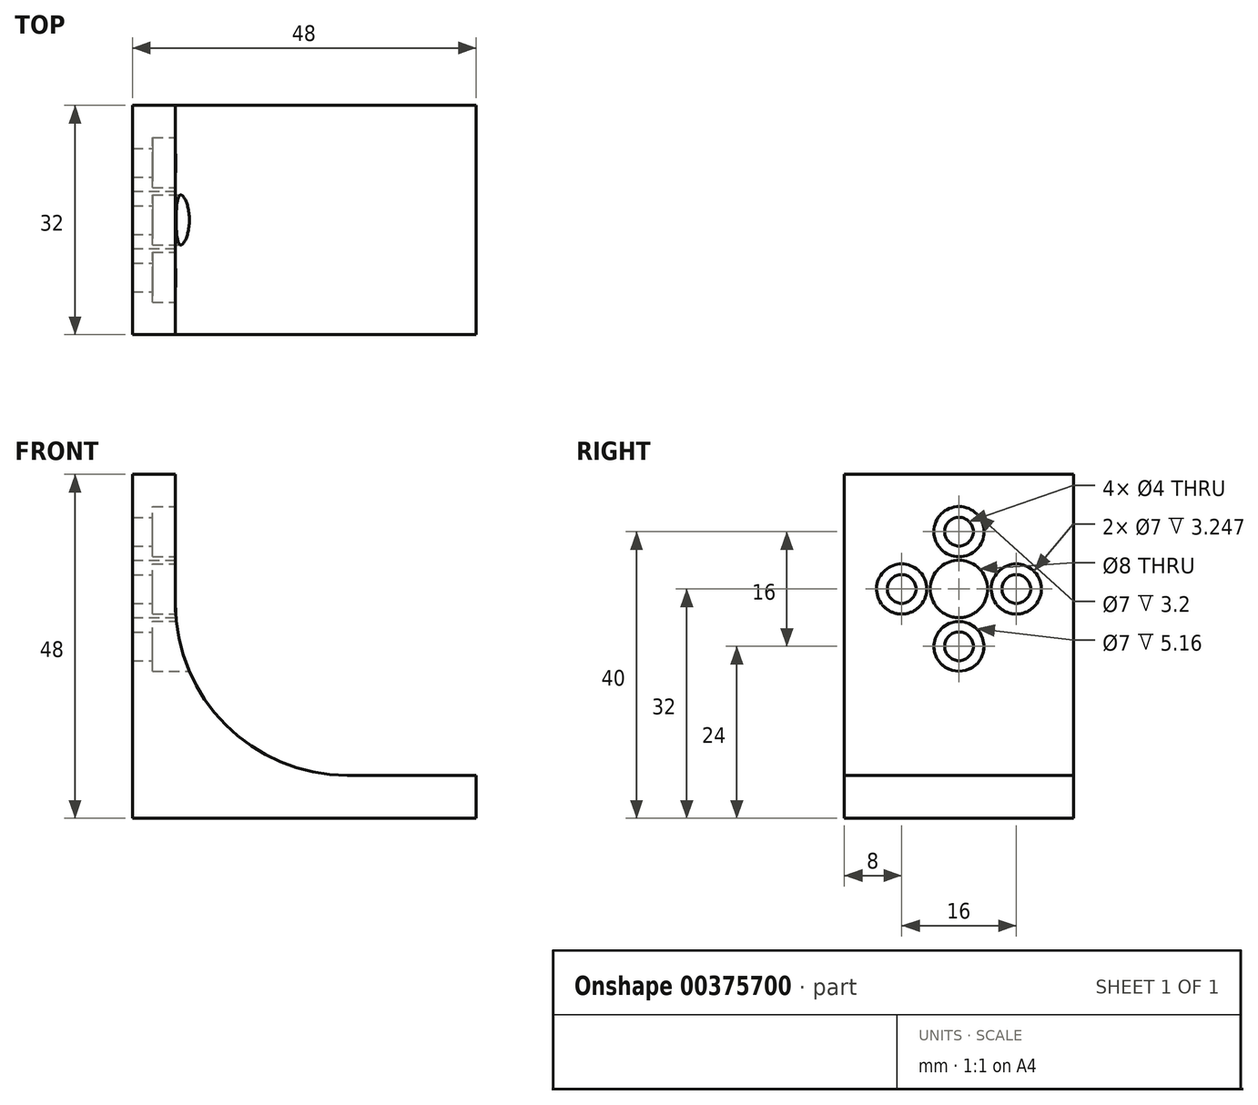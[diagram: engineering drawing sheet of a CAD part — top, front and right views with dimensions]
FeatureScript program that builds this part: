
annotation { "Feature Type Name" : "Feature", "Feature Type Description" : "" }
export const myFeature = defineFeature(function(context is Context, id is Id, definition is map)
    precondition{}
    {
        {
            assignVariable(context, id + "F0", {"name" : "Extrusion", "anyValue" : 0.4});
        }
        {
            assignVariable(context, id + "F1", {"name" : "Shells", "anyValue" : 3});
        }
        {
            assignVariable(context, id + "F2", {"name" : "Wall", "anyValue" : getVariable(context, 'Extrusion') * (getVariable(context, 'Shells') * 2 + 1)});
        }
        {
            assignVariable(context, id + "F3", {"name" : "Frame", "anyValue" : 6});
        }
        {
            var Q0;
            Q0=qCreatedBy(makeId("Front.planeOp"),FACE);
            var sketch = newSketch(context, id + "F4", { "sketchPlane" : qUnion([Q0])});
            skLineSegment(sketch, "E0", {"start": v(0, 48) * mm, "end": v(0, 0) * mm});
            skLineSegment(sketch, "E1", {"start": v(0, 0) * mm, "end": v(48, 0) * mm});
            skCircle(sketch, "E2", {"center": v(0, 0) * mm, "radius": 4 * mm, "construction": true});
            skCircle(sketch, "E3", {"center": v(16, 0) * mm, "radius": 4 * mm, "construction": true});
            skCircle(sketch, "E4", {"center": v(32, 0) * mm, "radius": 4 * mm, "construction": true});
            skCircle(sketch, "E5", {"center": v(0, 16) * mm, "radius": 4 * mm, "construction": true});
            skCircle(sketch, "E6", {"center": v(0, 32) * mm, "radius": 4 * mm, "construction": true});
            skLineSegment(sketch, "E7", {"start": v(0, 48) * mm, "end": v(6, 48) * mm});
            skLineSegment(sketch, "E8", {"start": v(48, 0) * mm, "end": v(48, 6) * mm});
            skArc(sketch, "E9", {"start": v(6, 48) * mm, "mid": v(18.3, 18.3) * mm, "end": v(48, 6) * mm});
            skLineSegment(sketch, "E10", {"start": v(6, 48) * mm, "end": v(6, 6) * mm});
            skLineSegment(sketch, "E11", {"start": v(6, 6) * mm, "end": v(48, 6) * mm});
            skSolve(sketch);
        }
        {
            var Q0;
            Q0=makeQuery(id+"F4.imprint","IMPRINT",FACE,{"disambiguationData":[TD([[makeQuery(id+"F4.imprint","IMPRINT",EDGE,{"derivedFrom":sQuery(id+"F4.wireOp",EDGE,"E0")}),1.0]])]});
            extrude(context, id + "F5", {"entities" : qUnion([Q0]), "endBound" : BoundingType.SYMMETRIC, "depth" : 32 * mm});
        }
        {
            var Q0;
            Q0=makeQuery(id+"F5.opExtrude","SWEPT_FACE",FACE,{"disambiguationData":[OSD([sQuery(id+"F4.wireOp",EDGE,"E10")])]});
            var sketch = newSketch(context, id + "F6", { "sketchPlane" : qUnion([Q0])});
            skPoint(sketch, "E12.0", {"position": v(0, 32) * mm});
            skCircle(sketch, "E13", {"center": v(0, 32) * mm, "radius": 4 * mm});
            skCircle(sketch, "E14", {"center": v(0, 40) * mm, "radius": 2 * mm});
            skCircle(sketch, "E15.1.0", {"center": v(-8, 32) * mm, "radius": 2 * mm});
            skCircle(sketch, "E15.2.0", {"center": v(0, 24) * mm, "radius": 2 * mm});
            skCircle(sketch, "E15.3.0", {"center": v(8, 32) * mm, "radius": 2 * mm});
            skCircle(sketch, "E16", {"center": v(0, 40) * mm, "radius": 3.5 * mm});
            skCircle(sketch, "E17", {"center": v(8, 32) * mm, "radius": 3.5 * mm});
            skCircle(sketch, "E18", {"center": v(0, 24) * mm, "radius": 3.5 * mm});
            skCircle(sketch, "E19", {"center": v(-8, 32) * mm, "radius": 3.5 * mm});
            skSolve(sketch);
        }
        {
            var Q0;
            Q0=makeQuery(id+"F5.opExtrude","SWEPT_EDGE",EDGE,{"disambiguationData":[OSD([sQuery(id+"F4.wireOp",EDGE,"E10"),sQuery(id+"F4.wireOp",EDGE,"E11")])]});
            fillet(context, id + "F7", {"entities" : qUnion([Q0]), "radius" : (getVariable(context, 'Frame') * 4) * mm, "tangentPropagation" : true, "allowEdgeOverflow" : false});
        }
        {
            var Q0;
            Q0=makeQuery(id+"F6.imprint","IMPRINT",FACE,{"disambiguationData":[TD([[makeQuery(id+"F6.imprint","IMPRINT",EDGE,{"derivedFrom":sQuery(id+"F6.wireOp",EDGE,"E15.1.0")}),1.0]])]});
            var Q1;
            Q1=makeQuery(id+"F6.imprint","IMPRINT",FACE,{"disambiguationData":[TD([[makeQuery(id+"F6.imprint","IMPRINT",EDGE,{"derivedFrom":sQuery(id+"F6.wireOp",EDGE,"E14")}),1.0]])]});
            var Q2;
            Q2=makeQuery(id+"F6.imprint","IMPRINT",FACE,{"disambiguationData":[TD([[makeQuery(id+"F6.imprint","IMPRINT",EDGE,{"derivedFrom":sQuery(id+"F6.wireOp",EDGE,"E15.3.0")}),1.0]])]});
            var Q3;
            Q3=makeQuery(id+"F6.imprint","IMPRINT",FACE,{"disambiguationData":[TD([[makeQuery(id+"F6.imprint","IMPRINT",EDGE,{"derivedFrom":sQuery(id+"F6.wireOp",EDGE,"E13")}),1.0]])]});
            var Q4;
            Q4=makeQuery(id+"F6.imprint","IMPRINT",FACE,{"disambiguationData":[TD([[makeQuery(id+"F6.imprint","IMPRINT",EDGE,{"derivedFrom":sQuery(id+"F6.wireOp",EDGE,"E15.2.0")}),1.0]])]});
            extrude(context, id + "F8", {"entities" : qUnion([Q0, Q1, Q2, Q3, Q4]), "operationType" : NewBodyOperationType.REMOVE, "endBound" : BoundingType.THROUGH_ALL, "oppositeDirection" : true, "depth" : 25 * mm, "hasSecondDirection" : true, "secondDirectionBound" : SecondDirectionBoundingType.THROUGH_ALL, "secondDirectionOppositeDirection" : false, "secondDirectionDepth" : 25 * mm});
        }
        {
            var Q0;
            {var subQ0=sQuery(id+"F6.wireOp",EDGE,"E15.1.0");Q0=makeQuery(id+"F6.imprint","IMPRINT",FACE,{"disambiguationData":[TD([[makeQuery(id+"F6.imprint","IMPRINT",EDGE,{"derivedFrom":subQ0}),-1.0]])]});}
            var Q1;
            {var subQ0=sQuery(id+"F6.wireOp",EDGE,"E19");var subQ1=sQuery(id+"F4.wireOp",EDGE,"E0");var subQ2=makeQuery(id+"FzLZcs18jVHRiGl_1.opShell","OFFSET_EDGE",EDGE,{"disambiguationData":[OSD([subQ1]),TDD([makeQuery(id+"F5.opExtrude","CAP_EDGE",EDGE,{"disambiguationData":[OSD([subQ1])],"isStart":false})])]});var subQ3=makeQuery(id+"F6.imprint","INTERSECT",VERTEX,{"disambiguationData":[OD(0.0)],"derivedFrom":[subQ2,subQ0]});Q1=makeQuery(id+"F6.imprint","IMPRINT",FACE,{"disambiguationData":[TD([[makeQuery(id+"F6.imprint","IMPRINT",EDGE,{"disambiguationData":[TD([[subQ3,-1.0]])],"derivedFrom":subQ0}),1.0]])]});}
            var Q2;
            Q2=makeQuery(id+"F6.imprint","IMPRINT",FACE,{"disambiguationData":[TD([[makeQuery(id+"F6.imprint","IMPRINT",EDGE,{"derivedFrom":sQuery(id+"F6.wireOp",EDGE,"E14")}),-1.0]])]});
            var Q3;
            {var subQ0=sQuery(id+"F6.wireOp",EDGE,"E15.3.0");Q3=makeQuery(id+"F6.imprint","IMPRINT",FACE,{"disambiguationData":[TD([[makeQuery(id+"F6.imprint","IMPRINT",EDGE,{"derivedFrom":subQ0}),-1.0]])]});}
            var Q4;
            {var subQ0=sQuery(id+"F6.wireOp",EDGE,"E17");var subQ1=sQuery(id+"F4.wireOp",EDGE,"E0");var subQ2=makeQuery(id+"FzLZcs18jVHRiGl_1.opShell","OFFSET_EDGE",EDGE,{"disambiguationData":[OSD([subQ1]),TDD([makeQuery(id+"F5.opExtrude","CAP_EDGE",EDGE,{"disambiguationData":[OSD([subQ1])],"isStart":true})])]});var subQ3=makeQuery(id+"F6.imprint","INTERSECT",VERTEX,{"disambiguationData":[OD(0.0)],"derivedFrom":[subQ2,subQ0]});Q4=makeQuery(id+"F6.imprint","IMPRINT",FACE,{"disambiguationData":[TD([[makeQuery(id+"F6.imprint","IMPRINT",EDGE,{"disambiguationData":[TD([[subQ3,1.0]])],"derivedFrom":subQ0}),1.0]])]});}
            var Q5;
            Q5=makeQuery(id+"F6.imprint","IMPRINT",FACE,{"disambiguationData":[TD([[makeQuery(id+"F6.imprint","IMPRINT",EDGE,{"derivedFrom":sQuery(id+"F6.wireOp",EDGE,"E15.2.0")}),-1.0]])]});
            extrude(context, id + "F9", {"entities" : qUnion([Q0, Q1, Q2, Q3, Q4, Q5]), "operationType" : NewBodyOperationType.REMOVE, "oppositeDirection" : true, "depth" : (getVariable(context, 'Frame') - getVariable(context, 'Wall')) * mm, "hasSecondDirection" : true, "secondDirectionBound" : SecondDirectionBoundingType.THROUGH_ALL, "secondDirectionOppositeDirection" : false, "secondDirectionDepth" : 25 * mm});
        }
    });
